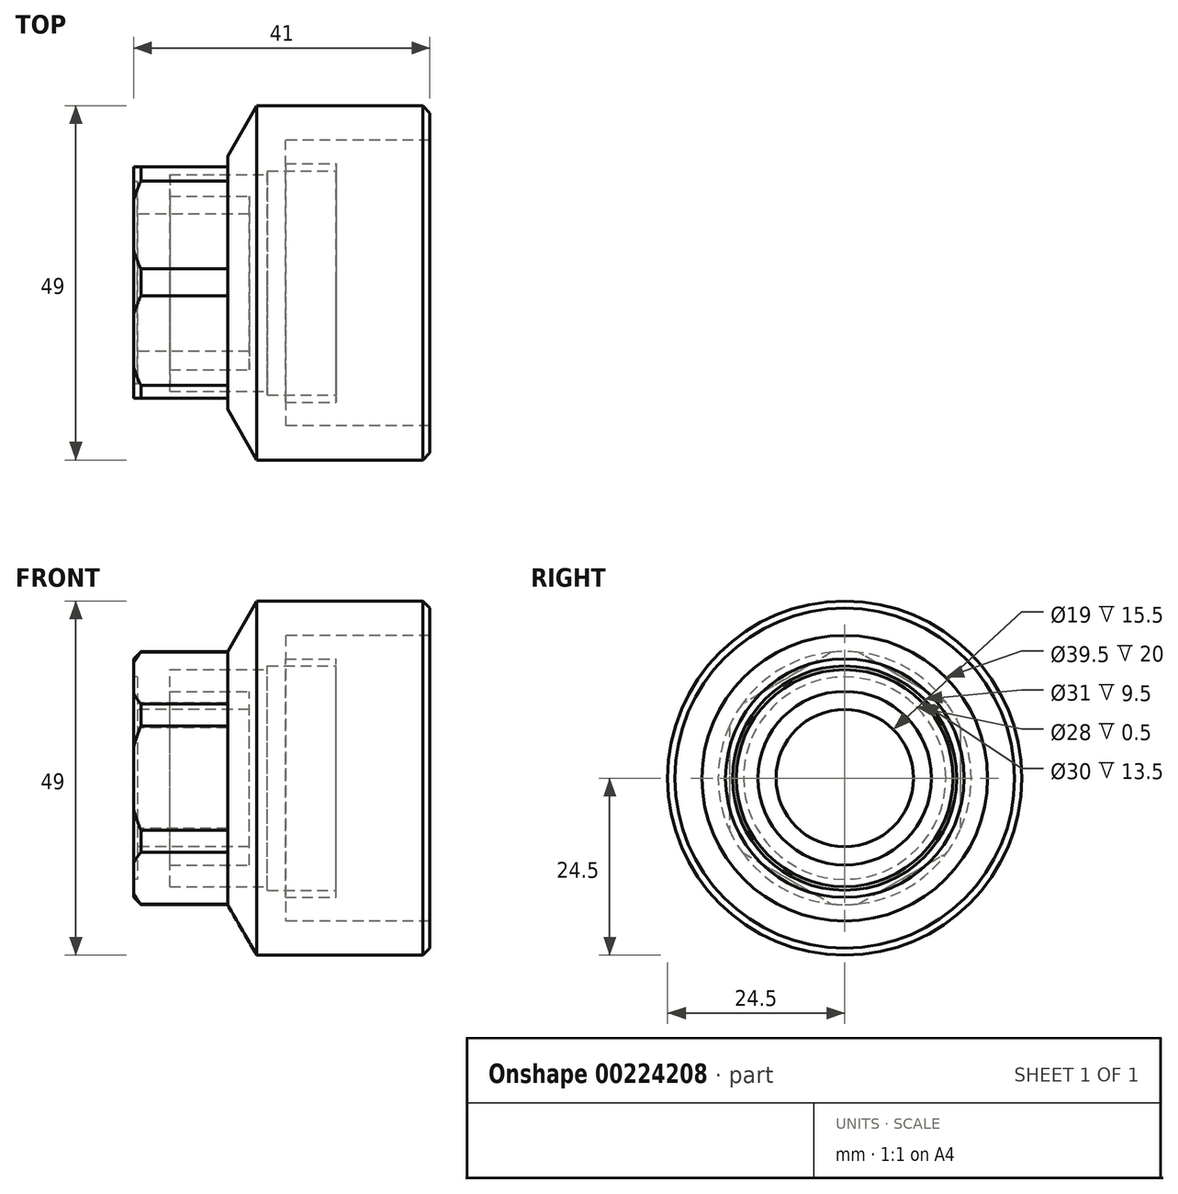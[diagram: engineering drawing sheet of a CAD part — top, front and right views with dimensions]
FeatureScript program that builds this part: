
annotation { "Feature Type Name" : "Feature", "Feature Type Description" : "" }
export const myFeature = defineFeature(function(context is Context, id is Id, definition is map)
    precondition{}
    {
        {
            var Q0;
            Q0=qCreatedBy(makeId("Front.planeOp"),FACE);
            var sketch = newSketch(context, id + "F0", { "sketchPlane" : qUnion([Q0])});
            skLineSegment(sketch, "E0", {"start": v(-15.78, 0) * mm, "end": v(17.8, 0) * mm, "construction": true});
            skLineSegment(sketch, "E1", {"start": v(0, 24.5) * mm, "end": v(-28, 24.5) * mm});
            skLineSegment(sketch, "E2", {"start": v(-28, 24.5) * mm, "end": v(-28, 17.5) * mm});
            skLineSegment(sketch, "E3", {"start": v(-28, 17.5) * mm, "end": v(-41, 17.5) * mm});
            skLineSegment(sketch, "E4", {"start": v(-41, 17.5) * mm, "end": v(-41, 9.5) * mm});
            skLineSegment(sketch, "E5", {"start": v(0, 19.75) * mm, "end": v(0, 24.5) * mm});
            skPoint(sketch, "E6.start.orphan", {"position": v(0, 18.06) * mm});
            skPoint(sketch, "E7.orphan", {"position": v(0, 9.38) * mm});
            skLineSegment(sketch, "E8", {"start": v(0, 19.75) * mm, "end": v(-13, 19.75) * mm});
            skLineSegment(sketch, "E9", {"start": v(-13, 19.75) * mm, "end": v(-13, 9.5) * mm});
            skLineSegment(sketch, "E10", {"start": v(-13, 9.5) * mm, "end": v(-34.07, 9.5) * mm});
            skLineSegment(sketch, "E11", {"start": v(-34.07, 9.5) * mm, "end": v(-41, 9.5) * mm});
            skSolve(sketch);
        }
        {
            var Q0;
            Q0 = qSketchRegion(id + "F0", true);
            var Q1;
            Q1=sQuery(id+"F0.wireOp",EDGE,"E0");
            revolve(context, id + "F1", {"entities" : qUnion([Q0]), "axis" : qUnion([Q1]), "revolveType" : RevolveType.FULL});
        }
        {
            var Q0;
            Q0=qCreatedBy(makeId("Right.planeOp"),FACE);
            var sketch = newSketch(context, id + "F2", { "sketchPlane" : qUnion([Q0])});
            skCircle(sketch, "E12", {"center": v(0, 0) * mm, "radius": 19.75 * mm});
            skCircle(sketch, "E13", {"center": v(0, 0) * mm, "radius": 16.5 * mm});
            skSolve(sketch);
        }
        {
            var Q0;
            Q0=makeQuery(id+"F2.imprint","IMPRINT",FACE,{"disambiguationData":[TD([[makeQuery(id+"F2.imprint","IMPRINT",EDGE,{"derivedFrom":sQuery(id+"F2.wireOp",EDGE,"E12")}),1.0]])]});
            extrude(context, id + "F3", {"entities" : qUnion([Q0]), "operationType" : NewBodyOperationType.REMOVE, "oppositeDirection" : true, "depth" : 20 * mm});
        }
        {
            var Q0;
            Q0=qCreatedBy(makeId("Right.planeOp"),FACE);
            var sketch = newSketch(context, id + "F4", { "sketchPlane" : qUnion([Q0])});
            skCircle(sketch, "E14", {"center": v(0, 0) * mm, "radius": 15.5 * mm});
            skCircle(sketch, "E15", {"center": v(0, -0.4) * mm, "radius": 12 * mm});
            skSolve(sketch);
        }
        {
            var Q0;
            Q0=makeQuery(id+"F4.imprint","IMPRINT",FACE,{"disambiguationData":[TD([[makeQuery(id+"F4.imprint","IMPRINT",EDGE,{"derivedFrom":sQuery(id+"F4.wireOp",EDGE,"E14")}),1.0]])]});
            extrude(context, id + "F5", {"entities" : qUnion([Q0]), "operationType" : NewBodyOperationType.REMOVE, "oppositeDirection" : true, "depth" : 22.5 * mm});
        }
        {
            var Q0;
            Q0=makeQuery(id+"F1.opRevolve","SWEPT_FACE",FACE,{"disambiguationData":[OSD([sQuery(id+"F0.wireOp",EDGE,"E4")])]});
            cPlane(context, id + "F6", {"entities" : qUnion([Q0]), "cplaneType" : CPlaneType.OFFSET, "offset" : 0 * mm, "width" : 150 * mm, "height" : 150 * mm});
        }
        {
            var Q0;
            Q0=qCreatedBy(id+"F6.planeOp",FACE);
            var sketch = newSketch(context, id + "F7", { "sketchPlane" : qUnion([Q0])});
            skCircle(sketch, "E16.cCircle", {"center": v(-0.06, 0) * mm, "radius": 16 * mm, "construction": true});
            skLineSegment(sketch, "E16.0", {"start": v(-0.06, 18.48) * mm, "end": v(15.94, 9.24) * mm});
            skLineSegment(sketch, "E16.1", {"start": v(15.94, 9.24) * mm, "end": v(15.94, -9.24) * mm});
            skLineSegment(sketch, "E16.2", {"start": v(15.94, -9.24) * mm, "end": v(-0.06, -18.48) * mm});
            skLineSegment(sketch, "E16.3", {"start": v(-0.06, -18.48) * mm, "end": v(-16.06, -9.24) * mm});
            skLineSegment(sketch, "E16.4", {"start": v(-16.06, -9.24) * mm, "end": v(-16.06, 9.24) * mm});
            skLineSegment(sketch, "E16.5", {"start": v(-16.06, 9.24) * mm, "end": v(-0.06, 18.48) * mm});
            skPoint(sketch, "E16.0.midPoint", {"position": v(7.94, 13.86) * mm});
            skCircle(sketch, "E17", {"center": v(-0.06, 0) * mm, "radius": 17.6 * mm});
            skSolve(sketch);
        }
        {
            var Q0;
            {var subQ0=sQuery(id+"F7.wireOp",EDGE,"E17");var subQ1=sQuery(id+"F7.wireOp",EDGE,"E16.5");var subQ2=makeQuery(id+"F7.imprint","INTERSECT",VERTEX,{"disambiguationData":[OD(0.0)],"derivedFrom":[subQ1,subQ0]});Q0=makeQuery(id+"F7.imprint","IMPRINT",FACE,{"disambiguationData":[TD([[makeQuery(id+"F7.imprint","IMPRINT",EDGE,{"disambiguationData":[TD([[subQ2,-1.0]])],"derivedFrom":subQ1}),1.0]])]});}
            var Q1;
            {var subQ0=sQuery(id+"F7.wireOp",EDGE,"E17");var subQ1=sQuery(id+"F7.wireOp",EDGE,"E16.4");var subQ2=makeQuery(id+"F7.imprint","INTERSECT",VERTEX,{"disambiguationData":[OD(0.0)],"derivedFrom":[subQ1,subQ0]});Q1=makeQuery(id+"F7.imprint","IMPRINT",FACE,{"disambiguationData":[TD([[makeQuery(id+"F7.imprint","IMPRINT",EDGE,{"disambiguationData":[TD([[subQ2,-1.0]])],"derivedFrom":subQ1}),1.0]])]});}
            var Q2;
            {var subQ0=sQuery(id+"F7.wireOp",EDGE,"E17");var subQ1=sQuery(id+"F7.wireOp",EDGE,"E16.3");var subQ2=makeQuery(id+"F7.imprint","INTERSECT",VERTEX,{"disambiguationData":[OD(0.0)],"derivedFrom":[subQ1,subQ0]});Q2=makeQuery(id+"F7.imprint","IMPRINT",FACE,{"disambiguationData":[TD([[makeQuery(id+"F7.imprint","IMPRINT",EDGE,{"disambiguationData":[TD([[subQ2,-1.0]])],"derivedFrom":subQ1}),1.0]])]});}
            var Q3;
            {var subQ0=sQuery(id+"F7.wireOp",EDGE,"E17");var subQ1=sQuery(id+"F7.wireOp",EDGE,"E16.2");var subQ2=makeQuery(id+"F7.imprint","INTERSECT",VERTEX,{"disambiguationData":[OD(0.0)],"derivedFrom":[subQ1,subQ0]});Q3=makeQuery(id+"F7.imprint","IMPRINT",FACE,{"disambiguationData":[TD([[makeQuery(id+"F7.imprint","IMPRINT",EDGE,{"disambiguationData":[TD([[subQ2,-1.0]])],"derivedFrom":subQ1}),1.0]])]});}
            var Q4;
            {var subQ0=sQuery(id+"F7.wireOp",EDGE,"E17");var subQ1=sQuery(id+"F7.wireOp",EDGE,"E16.1");var subQ2=makeQuery(id+"F7.imprint","INTERSECT",VERTEX,{"disambiguationData":[OD(0.0)],"derivedFrom":[subQ1,subQ0]});Q4=makeQuery(id+"F7.imprint","IMPRINT",FACE,{"disambiguationData":[TD([[makeQuery(id+"F7.imprint","IMPRINT",EDGE,{"disambiguationData":[TD([[subQ2,-1.0]])],"derivedFrom":subQ1}),1.0]])]});}
            var Q5;
            {var subQ0=sQuery(id+"F7.wireOp",EDGE,"E17");var subQ1=sQuery(id+"F7.wireOp",EDGE,"E16.0");var subQ2=makeQuery(id+"F7.imprint","INTERSECT",VERTEX,{"disambiguationData":[OD(0.0)],"derivedFrom":[subQ1,subQ0]});Q5=makeQuery(id+"F7.imprint","IMPRINT",FACE,{"disambiguationData":[TD([[makeQuery(id+"F7.imprint","IMPRINT",EDGE,{"disambiguationData":[TD([[subQ2,-1.0]])],"derivedFrom":subQ1}),1.0]])]});}
            extrude(context, id + "F8", {"entities" : qUnion([Q0, Q1, Q2, Q3, Q4, Q5]), "operationType" : NewBodyOperationType.REMOVE, "oppositeDirection" : true, "depth" : 13 * mm});
        }
        {
            var Q0;
            Q0=makeQuery(id+"F1.opRevolve","SWEPT_EDGE",EDGE,{"disambiguationData":[OSD([sQuery(id+"F0.wireOp",EDGE,"E1"),sQuery(id+"F0.wireOp",EDGE,"E2")])]});
            chamfer(context, id + "F9", {"entities" : qUnion([Q0]), "chamferType" : ChamferType.OFFSET_ANGLE, "width" : 7 * mm, "oppositeDirection" : false, "angle" : 30 * degree, "tangentPropagation" : true});
        }
        {
            var Q0;
            Q0=makeQuery(id+"F1.opRevolve","SWEPT_EDGE",EDGE,{"disambiguationData":[OSD([sQuery(id+"F0.wireOp",EDGE,"E1"),sQuery(id+"F0.wireOp",EDGE,"E5")])]});
            chamfer(context, id + "F10", {"entities" : qUnion([Q0]), "chamferType" : ChamferType.OFFSET_ANGLE, "width" : 1 * mm, "oppositeDirection" : false, "angle" : 45 * degree, "tangentPropagation" : true});
        }
        {
            var Q0;
            Q0=qCreatedBy(id+"F6.planeOp",FACE);
            var sketch = newSketch(context, id + "F11", { "sketchPlane" : qUnion([Q0])});
            skCircle(sketch, "E18", {"center": v(0, 0) * mm, "radius": 14 * mm});
            skCircle(sketch, "E19", {"center": v(0, 0) * mm, "radius": 9.5 * mm});
            skSolve(sketch);
        }
        {
            var Q0;
            Q0=makeQuery(id+"F11.imprint","IMPRINT",FACE,{"disambiguationData":[TD([[makeQuery(id+"F11.imprint","IMPRINT",EDGE,{"derivedFrom":sQuery(id+"F11.wireOp",EDGE,"E18")}),1.0]])]});
            extrude(context, id + "F12", {"entities" : qUnion([Q0]), "operationType" : NewBodyOperationType.REMOVE, "oppositeDirection" : true, "depth" : .5 * mm});
        }
        {
            var Q0;
            {var subQ0=sQuery(id+"F0.wireOp",EDGE,"E3");var subQ1=sQuery(id+"F0.wireOp",EDGE,"E4");Q0=makeQuery(id+"F8.boolean.opBoolean","SPLIT",EDGE,{"disambiguationData":[TD([makeQuery(id+"F1.opRevolve","SWEPT_FACE",FACE,{"disambiguationData":[OSD([subQ0])]}),makeQuery(id+"F1.opRevolve","SWEPT_FACE",FACE,{"disambiguationData":[OSD([subQ1])]}),makeQuery(id+"F8.opExtrude","SWEPT_FACE",FACE,{"disambiguationData":[OSD([sQuery(id+"F7.wireOp",EDGE,"E16.0")])]}),makeQuery(id+"F8.opExtrude","SWEPT_FACE",FACE,{"disambiguationData":[OSD([sQuery(id+"F7.wireOp",EDGE,"E16.1")])]})])],"derivedFrom":makeQuery(id+"F1.opRevolve","SWEPT_EDGE",EDGE,{"disambiguationData":[OSD([subQ0,subQ1])]})});}
            var Q1;
            {var subQ0=sQuery(id+"F0.wireOp",EDGE,"E3");var subQ1=sQuery(id+"F0.wireOp",EDGE,"E4");Q1=makeQuery(id+"F8.boolean.opBoolean","SPLIT",EDGE,{"disambiguationData":[TD([makeQuery(id+"F1.opRevolve","SWEPT_FACE",FACE,{"disambiguationData":[OSD([subQ0])]}),makeQuery(id+"F1.opRevolve","SWEPT_FACE",FACE,{"disambiguationData":[OSD([subQ1])]}),makeQuery(id+"F8.opExtrude","SWEPT_FACE",FACE,{"disambiguationData":[OSD([sQuery(id+"F7.wireOp",EDGE,"E16.0")])]}),makeQuery(id+"F8.opExtrude","SWEPT_FACE",FACE,{"disambiguationData":[OSD([sQuery(id+"F7.wireOp",EDGE,"E16.5")])]})])],"derivedFrom":makeQuery(id+"F1.opRevolve","SWEPT_EDGE",EDGE,{"disambiguationData":[OSD([subQ0,subQ1])]})});}
            var Q2;
            {var subQ0=sQuery(id+"F0.wireOp",EDGE,"E3");var subQ1=sQuery(id+"F0.wireOp",EDGE,"E4");Q2=makeQuery(id+"F8.boolean.opBoolean","SPLIT",EDGE,{"disambiguationData":[TD([makeQuery(id+"F1.opRevolve","SWEPT_FACE",FACE,{"disambiguationData":[OSD([subQ0])]}),makeQuery(id+"F1.opRevolve","SWEPT_FACE",FACE,{"disambiguationData":[OSD([subQ1])]}),makeQuery(id+"F8.opExtrude","SWEPT_FACE",FACE,{"disambiguationData":[OSD([sQuery(id+"F7.wireOp",EDGE,"E16.4")])]}),makeQuery(id+"F8.opExtrude","SWEPT_FACE",FACE,{"disambiguationData":[OSD([sQuery(id+"F7.wireOp",EDGE,"E16.5")])]})])],"derivedFrom":makeQuery(id+"F1.opRevolve","SWEPT_EDGE",EDGE,{"disambiguationData":[OSD([subQ0,subQ1])]})});}
            var Q3;
            {var subQ0=sQuery(id+"F0.wireOp",EDGE,"E3");var subQ1=sQuery(id+"F0.wireOp",EDGE,"E4");Q3=makeQuery(id+"F8.boolean.opBoolean","SPLIT",EDGE,{"disambiguationData":[TD([makeQuery(id+"F1.opRevolve","SWEPT_FACE",FACE,{"disambiguationData":[OSD([subQ0])]}),makeQuery(id+"F1.opRevolve","SWEPT_FACE",FACE,{"disambiguationData":[OSD([subQ1])]}),makeQuery(id+"F8.opExtrude","SWEPT_FACE",FACE,{"disambiguationData":[OSD([sQuery(id+"F7.wireOp",EDGE,"E16.3")])]}),makeQuery(id+"F8.opExtrude","SWEPT_FACE",FACE,{"disambiguationData":[OSD([sQuery(id+"F7.wireOp",EDGE,"E16.4")])]})])],"derivedFrom":makeQuery(id+"F1.opRevolve","SWEPT_EDGE",EDGE,{"disambiguationData":[OSD([subQ0,subQ1])]})});}
            var Q4;
            {var subQ0=sQuery(id+"F0.wireOp",EDGE,"E3");var subQ1=sQuery(id+"F0.wireOp",EDGE,"E4");Q4=makeQuery(id+"F8.boolean.opBoolean","SPLIT",EDGE,{"disambiguationData":[TD([makeQuery(id+"F1.opRevolve","SWEPT_FACE",FACE,{"disambiguationData":[OSD([subQ0])]}),makeQuery(id+"F1.opRevolve","SWEPT_FACE",FACE,{"disambiguationData":[OSD([subQ1])]}),makeQuery(id+"F8.opExtrude","SWEPT_FACE",FACE,{"disambiguationData":[OSD([sQuery(id+"F7.wireOp",EDGE,"E16.2")])]}),makeQuery(id+"F8.opExtrude","SWEPT_FACE",FACE,{"disambiguationData":[OSD([sQuery(id+"F7.wireOp",EDGE,"E16.3")])]})])],"derivedFrom":makeQuery(id+"F1.opRevolve","SWEPT_EDGE",EDGE,{"disambiguationData":[OSD([subQ0,subQ1])]})});}
            var Q5;
            {var subQ0=sQuery(id+"F0.wireOp",EDGE,"E3");var subQ1=sQuery(id+"F0.wireOp",EDGE,"E4");Q5=makeQuery(id+"F8.boolean.opBoolean","SPLIT",EDGE,{"disambiguationData":[TD([makeQuery(id+"F1.opRevolve","SWEPT_FACE",FACE,{"disambiguationData":[OSD([subQ0])]}),makeQuery(id+"F1.opRevolve","SWEPT_FACE",FACE,{"disambiguationData":[OSD([subQ1])]}),makeQuery(id+"F8.opExtrude","SWEPT_FACE",FACE,{"disambiguationData":[OSD([sQuery(id+"F7.wireOp",EDGE,"E16.1")])]}),makeQuery(id+"F8.opExtrude","SWEPT_FACE",FACE,{"disambiguationData":[OSD([sQuery(id+"F7.wireOp",EDGE,"E16.2")])]})])],"derivedFrom":makeQuery(id+"F1.opRevolve","SWEPT_EDGE",EDGE,{"disambiguationData":[OSD([subQ0,subQ1])]})});}
            chamfer(context, id + "F13", {"entities" : qUnion([Q0, Q1, Q2, Q3, Q4, Q5]), "width" : 1 * mm, "tangentPropagation" : true});
        }
        {
            var Q0;
            Q0=qCreatedBy(makeId("Right.planeOp"),FACE);
            var sketch = newSketch(context, id + "F14", { "sketchPlane" : qUnion([Q0])});
            skCircle(sketch, "E20", {"center": v(0, 0) * mm, "radius": 13.57 * mm});
            skSolve(sketch);
        }
        {
            var Q0;
            Q0 = qSketchRegion(id + "F14", true);
            extrude(context, id + "F15", {"entities" : qUnion([Q0]), "operationType" : NewBodyOperationType.REMOVE, "oppositeDirection" : true, "depth" : 25 * mm});
        }
        {
            var Q0;
            Q0=qCreatedBy(makeId("Right.planeOp"),FACE);
            var sketch = newSketch(context, id + "F16", { "sketchPlane" : qUnion([Q0])});
            skCircle(sketch, "E21", {"center": v(0, 0) * mm, "radius": 12 * mm});
            skCircle(sketch, "E22", {"center": v(0, 0) * mm, "radius": 15 * mm});
            skSolve(sketch);
        }
        {
            var Q0;
            Q0 = qSketchRegion(id + "F16", true);
            extrude(context, id + "F17", {"entities" : qUnion([Q0]), "operationType" : NewBodyOperationType.REMOVE, "oppositeDirection" : true, "depth" : 36 * mm});
        }
    });
